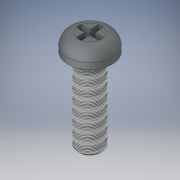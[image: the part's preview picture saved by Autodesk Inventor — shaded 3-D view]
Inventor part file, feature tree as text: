
AUTODESK INVENTOR PART (.ipt)
format: ipt  version: 2017 (Build 210142000, 142)  size: 150,016 bytes
history: native  units: in
note: dims shown in document units (in); Inventor stores cm internally (conversion verified against a paired STEP export)
features: extrude x3, sketch x3, fillet x1, thread x1, chamfer x1
ambient origin geometry x8: Origin, YZ Plane, XZ Plane, XY Plane, X Axis, Y Axis, Z Axis, Center Point
bodies: Solid1 (feature_tree)
feature tree (9):
  extrude  "Extrusion1"  Depth=0.3125in TaperAngle=0.0deg
  extrude  "Extrusion2"  Depth=0.062in TaperAngle=0.0deg
  fillet  "Fillet1"  Radius=0.04in
  thread  "Thread1"  [1 undecoded]
  chamfer  "Chamfer1"  Distance=0.01in Angle=45.0deg
  extrude  "Extrusion3"  Depth=0.05in TaperAngle=0.0deg
  sketch  "Sketch1"  dims[d0=0.092in d1=0.3125in d2=0.0in]
  sketch  "Sketch2"  dims[d3=0.167in d4=0.062in d5=0.0in d6=0.04in d7=1.0in d8=0.0in d9=0.01in d10=0.125in d11=45.0deg]
  sketch  "Sketch3"  dims[d12=0.02in d13=0.05in d14=0.0in]
note: 1 required parameter value undecoded (feature->parameter linkage not recoverable at this tier; creation-order binding heuristic only, values carry confidence <= 0.55)
